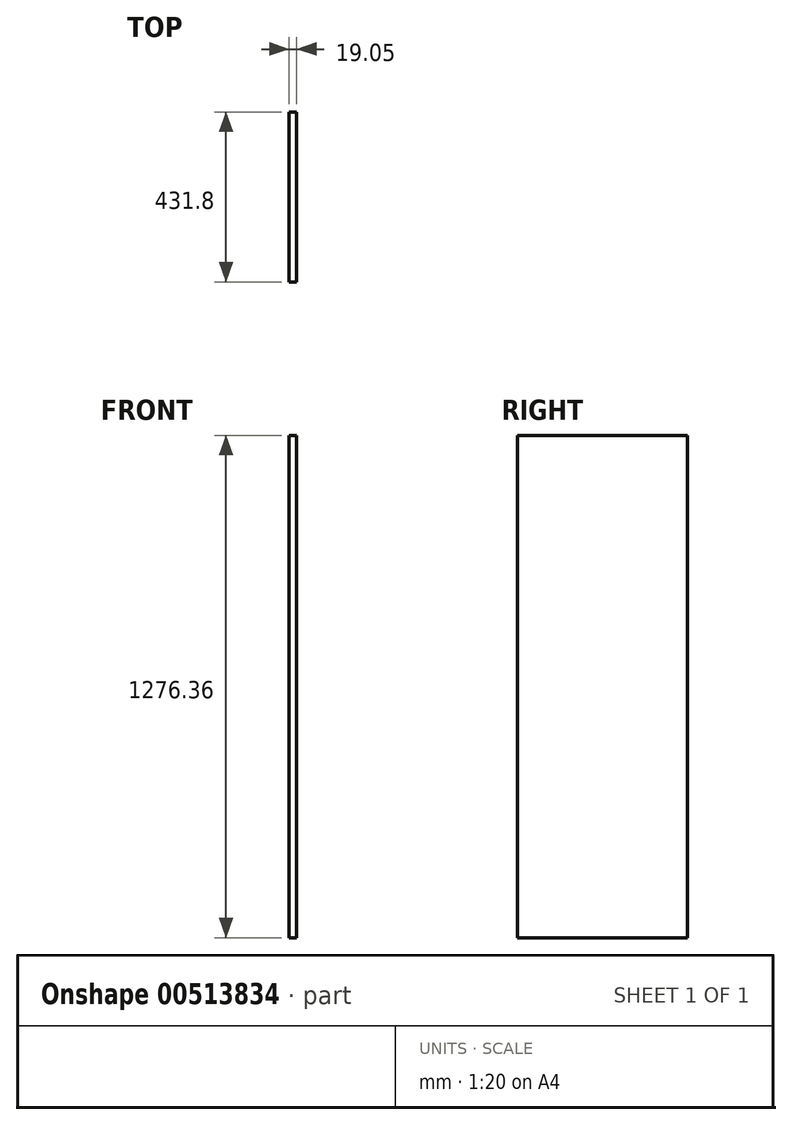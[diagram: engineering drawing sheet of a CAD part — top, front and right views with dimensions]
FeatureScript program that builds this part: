
annotation { "Feature Type Name" : "Feature", "Feature Type Description" : "" }
export const myFeature = defineFeature(function(context is Context, id is Id, definition is map)
    precondition{}
    {
        {
            var Q0;
            Q0=qCreatedBy(makeId("Right.planeOp"),FACE);
            var sketch = newSketch(context, id + "F0", { "sketchPlane" : qUnion([Q0])});
            skLineSegment(sketch, "E0.bottom", {"start": v(215.9, 638.17) * mm, "end": v(-215.9, 638.17) * mm});
            skLineSegment(sketch, "E0.top", {"start": v(215.9, -638.17) * mm, "end": v(-215.9, -638.17) * mm});
            skLineSegment(sketch, "E0.left", {"start": v(215.9, 638.18) * mm, "end": v(215.9, -638.17) * mm});
            skLineSegment(sketch, "E0.right", {"start": v(-215.9, 638.17) * mm, "end": v(-215.9, -638.17) * mm});
            skPoint(sketch, "E0.middle", {"position": v(0, 0) * mm});
            skSolve(sketch);
        }
        {
            var Q0;
            Q0 = qSketchRegion(id + "F0", true);
            extrude(context, id + "F1", {"entities" : qUnion([Q0]), "depth" : 19.05 * mm});
        }
    });
